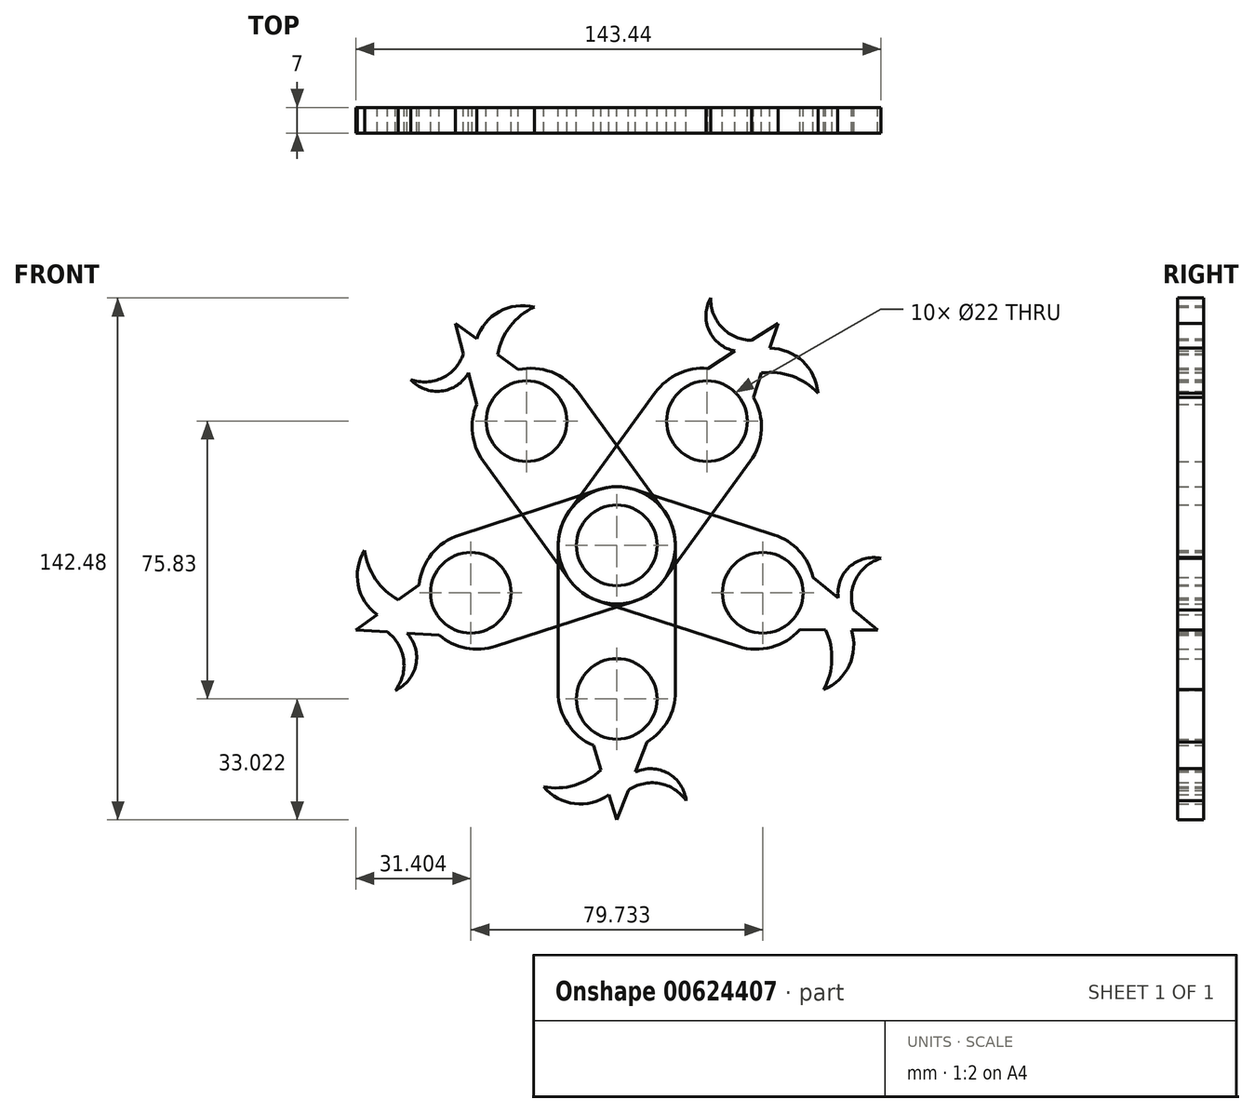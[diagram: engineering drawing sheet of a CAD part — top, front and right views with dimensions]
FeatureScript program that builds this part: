
annotation { "Feature Type Name" : "Feature", "Feature Type Description" : "" }
export const myFeature = defineFeature(function(context is Context, id is Id, definition is map)
    precondition{}
    {
        {
            var Q0;
            Q0=qCreatedBy(makeId("Front.planeOp"),FACE);
            var sketch = newSketch(context, id + "F0", { "sketchPlane" : qUnion([Q0])});
            skCircle(sketch, "E0", {"center": v(0, 0) * mm, "radius": 16 * mm});
            skCircle(sketch, "E1", {"center": v(0, -40) * mm, "radius": 16 * mm});
            skLineSegment(sketch, "E2", {"start": v(-16, 0) * mm, "end": v(-16, -40) * mm});
            skLineSegment(sketch, "E3", {"start": v(16, 0) * mm, "end": v(16, -40) * mm});
            skLineSegment(sketch, "E4", {"start": v(-6.42, -54.66) * mm, "end": v(0, -74.94) * mm});
            skLineSegment(sketch, "E5", {"start": v(0, -74.94) * mm, "end": v(8.3, -53.68) * mm});
            skArc(sketch, "E6", {"start": v(-20.01, -65.89) * mm, "mid": v(-11.52, -70.5) * mm, "end": v(-2.17, -68.08) * mm});
            skArc(sketch, "E7", {"start": v(-20.01, -65.89) * mm, "mid": v(-11.6, -65.52) * mm, "end": v(-4.31, -61.3) * mm});
            skArc(sketch, "E8", {"start": v(18.94, -69.73) * mm, "mid": v(14.03, -62.25) * mm, "end": v(5.1, -61.9) * mm});
            skArc(sketch, "E9", {"start": v(18.94, -69.73) * mm, "mid": v(11.63, -64.99) * mm, "end": v(3.13, -66.92) * mm});
            skSolve(sketch);
        }
        {
            var Q0;
            Q0 = qSketchRegion(id + "F0", true);
            extrude(context, id + "F1", {"entities" : qUnion([Q0]), "depth" : 7 * mm, "offsetDistance" : 25 * mm});
        }
        {
            var Q0;
            Q0=qCreatedBy(makeId("Front.planeOp"),FACE);
            var sketch = newSketch(context, id + "F2", { "sketchPlane" : qUnion([Q0])});
            skCircle(sketch, "E10", {"center": v(0, 0) * mm, "radius": 11 * mm});
            skCircle(sketch, "E11", {"center": v(0, -41.92) * mm, "radius": 11 * mm});
            skSolve(sketch);
        }
        {
            var Q0;
            Q0 = qSketchRegion(id + "F2", true);
            extrude(context, id + "F3", {"entities" : qUnion([Q0]), "operationType" : NewBodyOperationType.REMOVE, "endBound" : BoundingType.UP_TO_NEXT, "depth" : 25 * mm, "offsetDistance" : 25 * mm});
        }
        {
            var Q0;
            Q0=makeQuery(id+"F1.opExtrude","SWEPT_BODY",BODY,{"disambiguationData":[OSD([sQuery(id+"F0.wireOp",EDGE,"E0"),sQuery(id+"F0.wireOp",EDGE,"E1"),sQuery(id+"F0.wireOp",EDGE,"E2"),sQuery(id+"F0.wireOp",EDGE,"E3")])]});
            var Q1;
            Q1=makeQuery(id+"F1.opExtrude","SWEPT_FACE",FACE,{"disambiguationData":[OSD([sQuery(id+"F0.wireOp",EDGE,"E0")])]});
            circularPattern(context, id + "F4", {"entities" : qUnion([Q0]), "axis" : qUnion([Q1]), "angle" : 360 * degree, "instanceCount" : 5, "equalSpace" : true});
        }
    });
